# Revit family: Catch-Basin_MultiDrain_EconoDrain-Inline
name_source: partatom
category: Site
units: mm (PartAtom-declared; Revit-internal decimal feet)

## family parameters
Classification Number = 23.10.10.12
Cut with Voids When Loaded = No
Host = Face
Part Type = Normal
Round Connector Dimension = Use Diameter
Shared = No

## types (8) — shared parameters
Assembly Code = A1030600
Construction Details = http://www.arcat.com
Default Elevation = 0' - 0"
Downhill Trench Depth = 2' - 0"
Keynote = 02600
Manufacturer = MultiDrain Systems
Manufacturer Fax = 704-508-1011
Manufacturer Website = http://www.multidrainsystems.com
Maximum Run = 0' - 0"
Piping_Water Flow = 0 GPM
Product Data = http://www.arcat.com
Revision = R1_12_2013
Sales Information = http://www.multidrainsystems.com
Send Message = http://www.arcat.com
Specification = http://www.arcat.com
URL = http://www.multidrainsystems.com
Unit Length = 2' - 0"
Uphill Trench Depth = 2' - 0"
zero-valued in all types: Expected Lifespan (Years), Maintenance Schedule (Months), Warranty Duration (Years)

## per-type parameters (varying)
| type | Description | Grate Opening Width | Model | Trench Width | Unit Width | trenchrad |
| Series 24 | MultiDrain EconoDrain Inline Catch Basin - ECB2624 as Specified | 2' - 2 11/16" | ECB2624 | 1' - 11 15/16" | 2' - 7" | 0' - 11 31/32" |
| Series 18 | MultiDrain EconoDrain Inline Catch Basin - ECB1824 as Specified | 1' - 8 3/16" | ECB1824 | 1' - 5 15/16" | 2' - 0 1/2" | 0' - 8 31/32" |
| Series 15 | MultiDrain EconoDrain Inline Catch Basin - ECB1524 as Specified | 1' - 5 3/16" | ECB1524 | 1' - 2 15/16" | 1' - 9 1/2" | 0' - 7 15/32" |
| Series 12 | MultiDrain EconoDrain Inline Catch Basin - ECB1224 as Specified | 1' - 2 3/16" | ECB1224 | 0' - 11 15/16" | 1' - 6 1/2" | 0' - 5 31/32" |
| Series 10 | MultiDrain EconoDrain Inline Catch Basin - ECB1024 as Specified | 1' - 0 3/16" | ECB1024 | 0' - 9 15/16" | 1' - 4 1/2" | 0' - 4 31/32" |
| Series 8 | MultiDrain EconoDrain Inline Catch Basin - ECB0824 as Specified | 0' - 10 3/16" | ECB0824 | 0' - 7 15/16" | 1' - 2 1/2" | 0' - 3 31/32" |
| Series 6 | MultiDrain EconoDrain Inline Catch Basin - ECB0624 as Specified | 0' - 8 3/16" | ECB0624 | 0' - 5 15/16" | 1' - 0 1/2" | 0' - 2 31/32" |
| Series 4 | MultiDrain EconoDrain Inline Catch Basin - ECB0424 as Specified | 0' - 5 1/2" | ECB0424 | 0' - 3 15/16" | 0' - 10" | 0' - 1 31/32" |

## geometry (parser evidence)
native form markers: Sweep x4
no freeform markers — native parametric forms only
